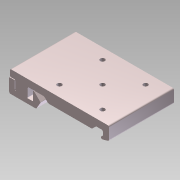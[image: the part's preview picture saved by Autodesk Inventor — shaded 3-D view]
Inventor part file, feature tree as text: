
AUTODESK INVENTOR PART (.ipt)
format: ipt  version: 2011 SP1 (Build 150282100, 282)  size: 401,408 bytes
history: native  units: mm
features: imported_body x11, thread x6, other x4
ambient origin geometry x8: Origin, YZ Plane, XZ Plane, XY Plane, X Axis, Y Axis, Z Axis, Center Point
feature tree (21):
  imported_body  "Base1"
  imported_body  "Base2"
  imported_body  "Base3"
  imported_body  "Base4"
  imported_body  "Base5"
  imported_body  "Base6"
  imported_body  "Base7"
  imported_body  "Base8"
  imported_body  "Base9"
  imported_body  "Base10"
  imported_body  "Base11"
  thread  "GEWINDEHUELSE"  [1 undecoded]
  thread  "GEWINDEHUELSE_1"  [1 undecoded]
  other  "SPANN"
  thread  "GEWINDEHUELSE_2"  [1 undecoded]
  other  "GEWSTIFT"
  thread  "GEWINDEHUELSE_3"  [1 undecoded]
  other  "SPANN_1"
  thread  "GEWINDEHUELSE_4"  [1 undecoded]
  other  "GEWSTIFT_1"
  thread  "GEWINDEHUELSE_5"  [1 undecoded]
note: 6 required parameter values undecoded (feature->parameter linkage not recoverable at this tier; creation-order binding heuristic only, values carry confidence <= 0.55)
